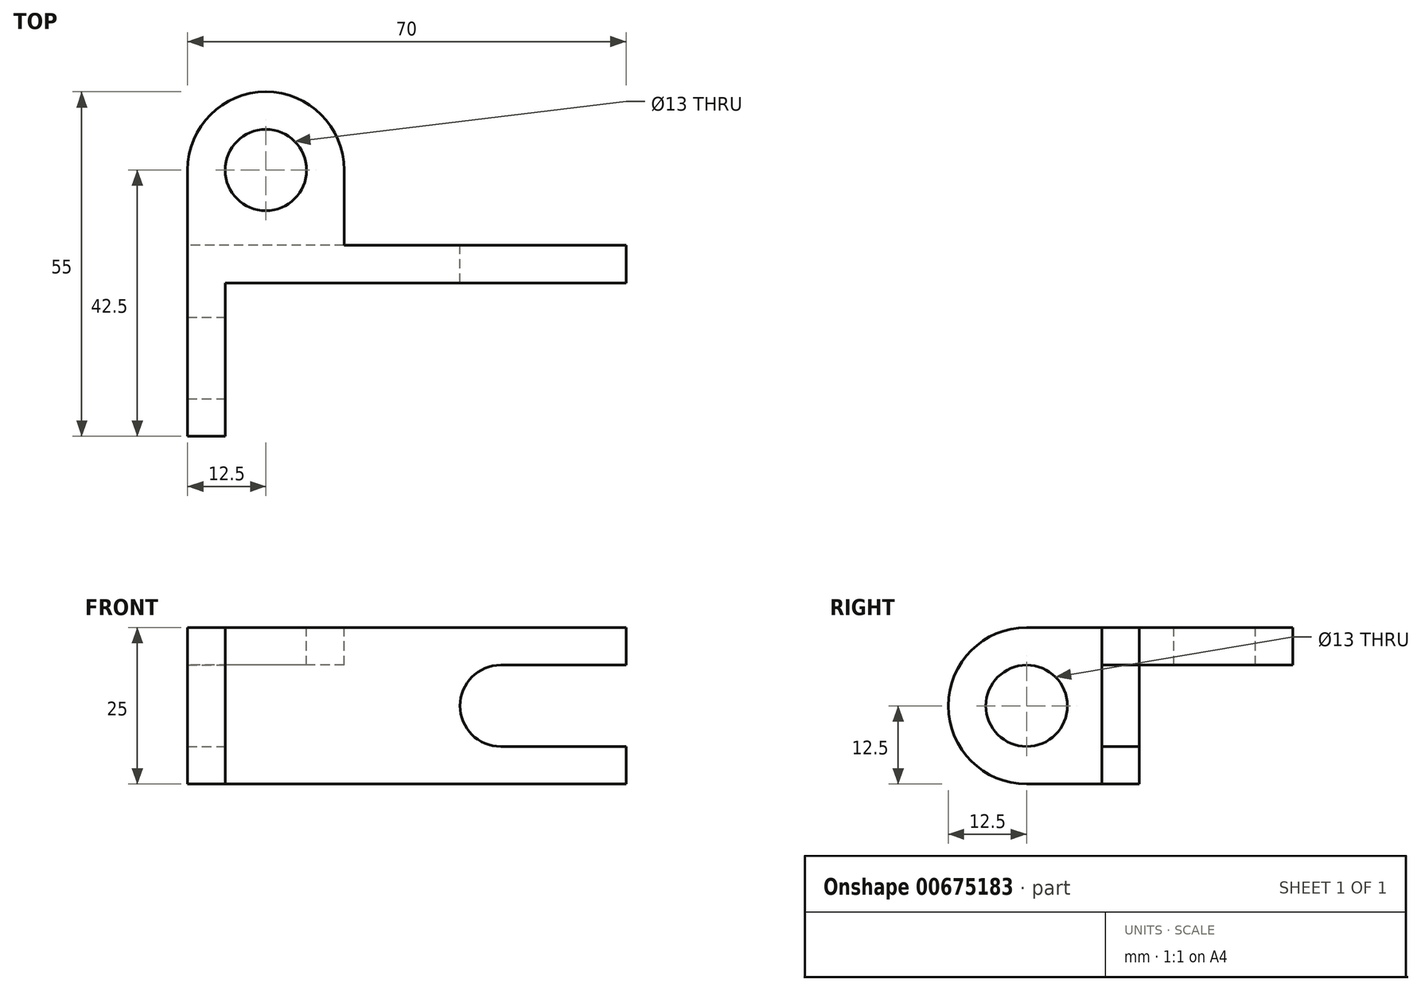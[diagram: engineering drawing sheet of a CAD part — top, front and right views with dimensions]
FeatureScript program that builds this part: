
annotation { "Feature Type Name" : "Feature", "Feature Type Description" : "" }
export const myFeature = defineFeature(function(context is Context, id is Id, definition is map)
    precondition{}
    {
        {
            var Q0;
            Q0=qCreatedBy(makeId("Front.planeOp"),FACE);
            var sketch = newSketch(context, id + "F0", { "sketchPlane" : qUnion([Q0])});
            skLineSegment(sketch, "E0.bottom", {"start": v(32, 12.5) * mm, "end": v(-32, 12.5) * mm});
            skLineSegment(sketch, "E0.top", {"start": v(32, -12.5) * mm, "end": v(-32, -12.5) * mm});
            skLineSegment(sketch, "E0.left", {"start": v(32, 12.5) * mm, "end": v(32, -12.5) * mm});
            skLineSegment(sketch, "E0.right", {"start": v(-32, 12.5) * mm, "end": v(-32, -12.5) * mm});
            skPoint(sketch, "E0.middle", {"position": v(0, 0) * mm});
            skLineSegment(sketch, "E1.bottom", {"start": v(32, 6.5) * mm, "end": v(12, 6.5) * mm});
            skLineSegment(sketch, "E1.top", {"start": v(32, -6.5) * mm, "end": v(12, -6.5) * mm});
            skLineSegment(sketch, "E1.left", {"start": v(32, 6.5) * mm, "end": v(32, -6.5) * mm});
            skLineSegment(sketch, "E1.right", {"start": v(12, 6.5) * mm, "end": v(12, -6.5) * mm});
            skPoint(sketch, "E1.middle", {"position": v(22, 0) * mm});
            skCircle(sketch, "E2", {"center": v(12, 0) * mm, "radius": 6.5 * mm});
            skSolve(sketch);
        }
        {
            var Q0;
            {var subQ4=sQuery(id+"F0.wireOp",EDGE,"E0.bottom");Q0=makeQuery(id+"F0.imprint","IMPRINT",FACE,{"disambiguationData":[TD([[makeQuery(id+"F0.imprint","IMPRINT",EDGE,{"derivedFrom":subQ4}),1.0]])]});}
            extrude(context, id + "F1", {"entities" : qUnion([Q0]), "depth" : 6 * mm, "offsetDistance" : 25 * mm});
        }
        {
            var Q0;
            Q0=makeQuery(id+"F1.opExtrude","SWEPT_FACE",FACE,{"disambiguationData":[OSD([sQuery(id+"F0.wireOp",EDGE,"E0.right")])]});
            var sketch = newSketch(context, id + "F2", { "sketchPlane" : qUnion([Q0])});
            skLineSegment(sketch, "E3.bottom", {"start": v(0, 12.5) * mm, "end": v(18, 12.5) * mm});
            skLineSegment(sketch, "E3.top", {"start": v(0, -12.5) * mm, "end": v(18, -12.5) * mm});
            skLineSegment(sketch, "E3.left", {"start": v(0, 12.5) * mm, "end": v(0, -12.5) * mm});
            skLineSegment(sketch, "E3.right", {"start": v(18, 12.5) * mm, "end": v(18, -12.5) * mm});
            skCircle(sketch, "E4", {"center": v(18, 0) * mm, "radius": 12.5 * mm});
            skCircle(sketch, "E5", {"center": v(18, 0) * mm, "radius": 6.5 * mm});
            skSolve(sketch);
        }
        {
            var Q0;
            Q0 = qSketchRegion(id + "F2", true);
            extrude(context, id + "F3", {"entities" : qUnion([Q0]), "operationType" : NewBodyOperationType.ADD, "depth" : 6 * mm, "offsetDistance" : 25 * mm});
        }
        {
            var Q0;
            Q0=makeQuery(id+"F3.boolean.opBoolean","MERGE",FACE,{"derivedFrom":[makeQuery(id+"F1.opExtrude","SWEPT_FACE",FACE,{"disambiguationData":[OSD([sQuery(id+"F0.wireOp",EDGE,"E0.bottom")])]}),makeQuery(id+"F3.opExtrude","SWEPT_FACE",FACE,{"disambiguationData":[OSD([sQuery(id+"F2.wireOp",EDGE,"E3.bottom")])]})]});
            var sketch = newSketch(context, id + "F4", { "sketchPlane" : qUnion([Q0])});
            skLineSegment(sketch, "E6.bottom", {"start": v(-38, -6) * mm, "end": v(-13, -6) * mm});
            skLineSegment(sketch, "E6.top", {"start": v(-38, 12) * mm, "end": v(-13, 12) * mm});
            skLineSegment(sketch, "E6.left", {"start": v(-38, -6) * mm, "end": v(-38, 12) * mm});
            skLineSegment(sketch, "E6.right", {"start": v(-13, -6) * mm, "end": v(-13, 12) * mm});
            skArc(sketch, "E7", {"start": v(-13, 12) * mm, "mid": v(-25.5, 24.5) * mm, "end": v(-38, 12) * mm});
            skSolve(sketch);
        }
        {
            var Q0;
            Q0=makeQuery(id+"F4.imprint","IMPRINT",FACE,{"disambiguationData":[TD([[makeQuery(id+"F4.imprint","IMPRINT",EDGE,{"derivedFrom":sQuery(id+"F4.wireOp",EDGE,"E6.top")}),1.0]])]});
            var Q1;
            {var subQ0=sQuery(id+"F4.wireOp",EDGE,"E6.left");var subQ1=sQuery(id+"F2.wireOp",EDGE,"E3.bottom");var subQ5=sQuery(id+"F4.wireOp",EDGE,"E6.bottom");var subQ6=makeQuery(id+"F4.imprint","INTERSECT",VERTEX,{"derivedFrom":[makeQuery(id+"F3.opExtrude","CAP_EDGE",EDGE,{"disambiguationData":[OSD([subQ1])],"isStart":false}),subQ5,subQ0]});Q1=makeQuery(id+"F4.imprint","IMPRINT",FACE,{"disambiguationData":[TD([[makeQuery(id+"F4.imprint","IMPRINT",EDGE,{"disambiguationData":[TD([[subQ6,-1.0]])],"derivedFrom":subQ5}),1.0]])]});}
            var Q2;
            {var subQ0=sQuery(id+"F4.wireOp",EDGE,"E6.top");Q2=makeQuery(id+"F4.imprint","IMPRINT",FACE,{"disambiguationData":[TD([[makeQuery(id+"F4.imprint","IMPRINT",EDGE,{"derivedFrom":subQ0}),-1.0]])]});}
            extrude(context, id + "F5", {"entities" : qUnion([Q0, Q1, Q2]), "operationType" : NewBodyOperationType.ADD, "oppositeDirection" : true, "depth" : 6 * mm, "offsetDistance" : 25 * mm});
        }
        {
            var Q0;
            Q0=sQuery(id+"F4.wireOp",VERTEX,"E7.center");
            var Q1;
            Q1=makeQuery(id+"F1.opExtrude","SWEPT_BODY",BODY,{"disambiguationData":[OSD([sQuery(id+"F0.wireOp",EDGE,"E0.bottom"),sQuery(id+"F0.wireOp",EDGE,"E0.top"),sQuery(id+"F0.wireOp",EDGE,"E0.left"),sQuery(id+"F0.wireOp",EDGE,"E0.right"),sQuery(id+"F0.wireOp",EDGE,"E1.bottom"),sQuery(id+"F0.wireOp",EDGE,"E1.top"),sQuery(id+"F0.wireOp",EDGE,"E2")])]});
            hole(context, id + "F6", {"style" : HoleStyle.SIMPLE, "endStyle" : HoleEndStyle.THROUGH, "holeDiameter" : 13 * mm, "majorDiameter" : 5 * mm, "isTappedThrough" : true, "tappedDepth" : 12 * mm, "tapClearance" : 3, "locations" : qUnion([Q0]), "scope" : qUnion([Q1])});
        }
    });
